# Revit family: Tables-Meeting-Teknion-BC_CWA_Workshop_Conference_Table-R2018
name_source: partatom
category: Furniture
revit_build: Autodesk Revit 2018 (Build: 20190510_1515(x64)
units: mm (PartAtom-declared; Revit-internal decimal feet)

## family parameters
Always vertical = Yes
Cut with Voids When Loaded = No
OmniClass Number = 23.40.20.00
OmniClass Title = General Furniture and Specialties
Room Calculation Point = No
Shared = Yes
Work Plane-Based = No

## types (7) — shared parameters
Assembly Code = E2020200
Manufacturer = Teknion
Manufacturer Fax = 416.661.4586
Part Number = BC_CWA
Product Documentation Link = https://www.teknion.com
Product Line = Expansion Casegoods
Product Page URL = https://www.teknion.com
Series = Expansion Casegoods
Sustainability Data = https://www.teknion.com
URL = www.teknion.com
Unit Weight URL = http://www.teknion.com
Warranty = http://www.teknion.com

## per-type parameters (varying)
| type | Depth | Description | Height | Leg Depth | Model |
| 1 3/16" Worksurface Thickness, 42" Depth | 41.79 " | Workshop Conference Table, 1 3/16" Worksurface Thickness, 42" Depth | 28.996 " | 7.709 " | BCMCWA42_____ |
| 1 9/16" Worksurface Thickness, 42" Depth | 41.79 " | Workshop Conference Table, 1 9/16" Worksurface Thickness, 42" Depth | 29.362 " | 7.709 " | BCXCWA42_____ |
| 1 3/16" Worksurface Thickness, 48" Depth | 47.76 " | Workshop Conference Table, 1 3/16" Worksurface Thickness, 48" Depth | 28.996 " | 7.709 " | BCMCWA48_____ |
| 1 3/16" Worksurface Thickness, 54" Depth | 53.73 " | Workshop Conference Table, 1 3/16" Worksurface Thickness, 54" Depth | 28.996 " | 11.709 " | BCMCWA54_____ |
| 1 3/16" Worksurface Thickness, 60" Depth | 59.7 " | Workshop Conference Table, 1 3/16" Worksurface Thickness, 60" Depth | 28.996 " | 11.709 " | BCMCWA60_____ |
| 1 9/16" Worksurface Thickness, 48" Depth | 47.76 " | Workshop Conference Table, 1 9/16" Worksurface Thickness, 48" Depth | 29.362 " | 7.709 " | BCXCWA48_____ |
| 1 9/16" Worksurface Thickness, 54" Depth | 53.73 " | Workshop Conference Table, 1 9/16" Worksurface Thickness, 54" Depth | 29.362 " | 11.709 " | BCXCWA54_____ |

## geometry (parser evidence)
native form markers: Blend x4, Sweep x3
no freeform markers — native parametric forms only
